FCSTD DOCUMENT  (FreeCAD 0.20R26155 (Git))
Label: PTS526 SKG15 SMTR2 LFS
License: All rights reserved
LicenseURL: http://en.wikipedia.org/wiki/All_rights_reserved
objects: Sketcher::SketchObject×1
note: 1 computed .brp shape members not serialized (recipe doc carries the construction recipe); baked Part::Feature solids carry a one-line shape summary decoded from their .brp

FEATURE [Sketcher::SketchObject] Sketch  label="Pads_TH_SMD"
  FullyConstrained = true
  sketch-geometry (21):
    g0: LineSegment StartX=0 StartY=0 StartZ=0 EndX=1 EndY=0 EndZ=0
    g1: LineSegment StartX=1 StartY=0 StartZ=0 EndX=1 EndY=0.7 EndZ=0
    g2: LineSegment StartX=1 StartY=0.7 StartZ=0 EndX=0 EndY=0.7 EndZ=0
    g3: LineSegment StartX=0 StartY=0.7 StartZ=0 EndX=0 EndY=0 EndZ=0
    g4: LineSegment StartX=0 StartY=3.7 StartZ=0 EndX=1 EndY=3.7 EndZ=0
    g5: LineSegment StartX=1 StartY=3.7 StartZ=0 EndX=1 EndY=4.4 EndZ=0
    g6: LineSegment StartX=1 StartY=4.4 StartZ=0 EndX=0 EndY=4.4 EndZ=0
    g7: LineSegment StartX=0 StartY=4.4 StartZ=0 EndX=0 EndY=3.7 EndZ=0
    g8: LineSegment StartX=6 StartY=0.7 StartZ=0 EndX=7 EndY=0.7 EndZ=0
    g9: LineSegment StartX=7 StartY=0.7 StartZ=0 EndX=7 EndY=0 EndZ=0
    g10: LineSegment StartX=7 StartY=0 StartZ=0 EndX=6 EndY=0 EndZ=0
    g11: LineSegment StartX=6 StartY=0 StartZ=0 EndX=6 EndY=0.7 EndZ=0
    g12: LineSegment StartX=6 StartY=3.7 StartZ=0 EndX=7 EndY=3.7 EndZ=0
    g13: LineSegment StartX=7 StartY=3.7 StartZ=0 EndX=7 EndY=4.4 EndZ=0
    g14: LineSegment StartX=7 StartY=4.4 StartZ=0 EndX=6 EndY=4.4 EndZ=0
    g15: LineSegment StartX=6 StartY=4.4 StartZ=0 EndX=6 EndY=3.7 EndZ=0
    g16: LineSegment StartX=1 StartY=0.7 StartZ=0 EndX=1 EndY=3.7 EndZ=0
    g17: LineSegment StartX=6 StartY=3.7 StartZ=0 EndX=6 EndY=0.7 EndZ=0
    g18: LineSegment StartX=7 StartY=3.7 StartZ=0 EndX=7 EndY=0.7 EndZ=0
    g19: LineSegment StartX=0 StartY=4.05 StartZ=0 EndX=7 EndY=4.05 EndZ=0
    g20: LineSegment StartX=0 StartY=0.35 StartZ=0 EndX=7 EndY=0.35 EndZ=0
  constraints (58):
    c: Coincident(g0,g1)
    c: Coincident(g1,g2)
    c: Coincident(g2,g3)
    c: Coincident(g3,g0)
    c: Horizontal(g0)
    c: Horizontal(g2)
    c: Vertical(g1)
    c: Vertical(g3)
    c: Coincident(g0,g-1)
    c: Coincident(g4,g5)
    c: Coincident(g5,g6)
    c: Coincident(g6,g7)
    c: Coincident(g7,g4)
    c: Horizontal(g4)
    c: Horizontal(g6)
    c: Vertical(g5)
    c: Vertical(g7)
    c: PointOnObject(g4,g-2)
    c: Coincident(g8,g9)
    c: Coincident(g9,g10)
    c: Coincident(g10,g11)
    c: Coincident(g11,g8)
    c: Horizontal(g8)
    c: Horizontal(g10)
    c: Vertical(g9)
    c: Vertical(g11)
    c: PointOnObject(g9,g-1)
    c: Coincident(g12,g13)
    c: Coincident(g13,g14)
    c: Coincident(g14,g15)
    c: Coincident(g15,g12)
    c: Horizontal(g12)
    c: Horizontal(g14)
    c: Vertical(g13)
    c: Vertical(g15)
    c: Equal(g3,g7)
    c: Equal(g7,g15)
    c: Equal(g15,g11)
    c: DistanceY(g3,g3) = 0.7
    c: Equal(g2,g6)
    c: Equal(g6,g14)
    c: Equal(g14,g8)
    c: Coincident(g16,g1)
    c: Coincident(g16,g4)
    c: Coincident(g17,g12)
    c: Coincident(g17,g8)
    c: Vertical(g17)
    c: DistanceX(g5,g14) = 5
    c: Coincident(g18,g12)
    c: Coincident(g18,g8)
    c: DistanceX(g6,g13) = 7
    c: Horizontal(g19)
    c: Symmetric(g13,g13,g19)
    c: Symmetric(g7,g7,g19)
    c: PointOnObject(g20,g9)
    c: Horizontal(g20)
    c: Symmetric(g3,g3,g20)
    c: DistanceY(g20,g19) = 3.7
